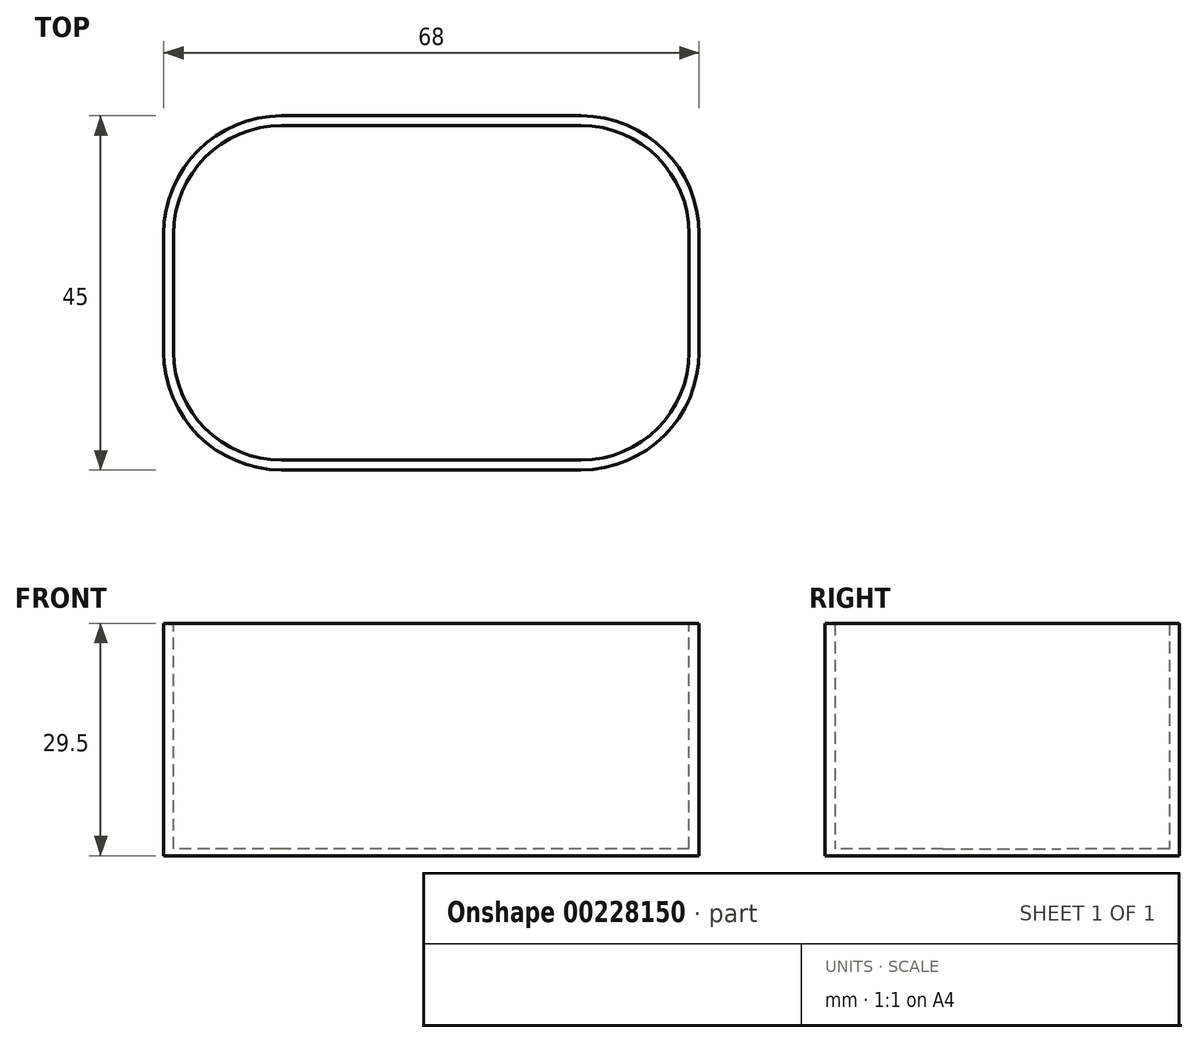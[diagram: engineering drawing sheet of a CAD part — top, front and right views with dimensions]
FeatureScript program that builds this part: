
annotation { "Feature Type Name" : "Feature", "Feature Type Description" : "" }
export const myFeature = defineFeature(function(context is Context, id is Id, definition is map)
    precondition{}
    {
        {
            assignVariable(context, id + "F0", {"name" : "Depth", "anyValue" : 29.5});
        }
        {
            assignVariable(context, id + "F1", {"name" : "WallThickness", "anyValue" : 1.25});
        }
        {
            var Q0;
            Q0=qCreatedBy(makeId("Top.planeOp"),FACE);
            var sketch = newSketch(context, id + "F2", { "sketchPlane" : qUnion([Q0])});
            skLineSegment(sketch, "E0.bottom", {"start": v(34, -22.5) * mm, "end": v(-34, -22.5) * mm});
            skLineSegment(sketch, "E0.top", {"start": v(34, 22.5) * mm, "end": v(-34, 22.5) * mm});
            skLineSegment(sketch, "E0.left", {"start": v(34, -22.5) * mm, "end": v(34, 22.5) * mm});
            skLineSegment(sketch, "E0.right", {"start": v(-34, -22.5) * mm, "end": v(-34, 22.5) * mm});
            skPoint(sketch, "E0.middle", {"position": v(0, 0) * mm});
            skSolve(sketch);
        }
        {
            var Q0;
            Q0=makeQuery(id+"F2.imprint","IMPRINT",FACE,{"disambiguationData":[TD([[makeQuery(id+"F2.imprint","IMPRINT",EDGE,{"derivedFrom":sQuery(id+"F2.wireOp",EDGE,"E0.bottom")}),-1.0]])]});
            extrude(context, id + "F3", {"entities" : qUnion([Q0]), "depth" : (getVariable(context, 'Depth')) * mm, "offsetDistance" : 25 * mm});
        }
        {
            var Q0;
            Q0=makeQuery(id+"F3.opExtrude","SWEPT_EDGE",EDGE,{"disambiguationData":[OSD([sQuery(id+"F2.wireOp",EDGE,"E0.bottom"),sQuery(id+"F2.wireOp",EDGE,"E0.left")])]});
            var Q1;
            Q1=makeQuery(id+"F3.opExtrude","SWEPT_EDGE",EDGE,{"disambiguationData":[OSD([sQuery(id+"F2.wireOp",EDGE,"E0.top"),sQuery(id+"F2.wireOp",EDGE,"E0.left")])]});
            var Q2;
            Q2=makeQuery(id+"F3.opExtrude","SWEPT_EDGE",EDGE,{"disambiguationData":[OSD([sQuery(id+"F2.wireOp",EDGE,"E0.bottom"),sQuery(id+"F2.wireOp",EDGE,"E0.right")])]});
            var Q3;
            Q3=makeQuery(id+"F3.opExtrude","SWEPT_EDGE",EDGE,{"disambiguationData":[OSD([sQuery(id+"F2.wireOp",EDGE,"E0.top"),sQuery(id+"F2.wireOp",EDGE,"E0.right")])]});
            fillet(context, id + "F4", {"entities" : qUnion([Q0, Q1, Q2, Q3]), "radius" : 15 * mm, "tangentPropagation" : true, "allowEdgeOverflow" : false});
        }
        {
            var Q0;
            Q0=makeQuery(id+"F3.opExtrude","CAP_FACE",FACE,{"disambiguationData":[OSD([sQuery(id+"F2.wireOp",EDGE,"E0.bottom"),sQuery(id+"F2.wireOp",EDGE,"E0.top"),sQuery(id+"F2.wireOp",EDGE,"E0.left"),sQuery(id+"F2.wireOp",EDGE,"E0.right")])],"isStart":false});
            shell(context, id + "F5", {"entities" : qUnion([Q0]), "thickness" : (getVariable(context, 'WallThickness')) * mm});
        }
        {
            var Q0;
            Q0=makeQuery(id+"F5.opShell","OFFSET_FACE",FACE,{"disambiguationData":[OSD([sQuery(id+"F2.wireOp",EDGE,"E0.bottom"),sQuery(id+"F2.wireOp",EDGE,"E0.top"),sQuery(id+"F2.wireOp",EDGE,"E0.left"),sQuery(id+"F2.wireOp",EDGE,"E0.right")])]});
            extrude(context, id + "F6", {"entities" : qUnion([Q0]), "operationType" : NewBodyOperationType.REMOVE, "oppositeDirection" : true, "depth" : (1.25 - 0.9) * mm, "offsetDistance" : 25 * mm});
        }
    });
